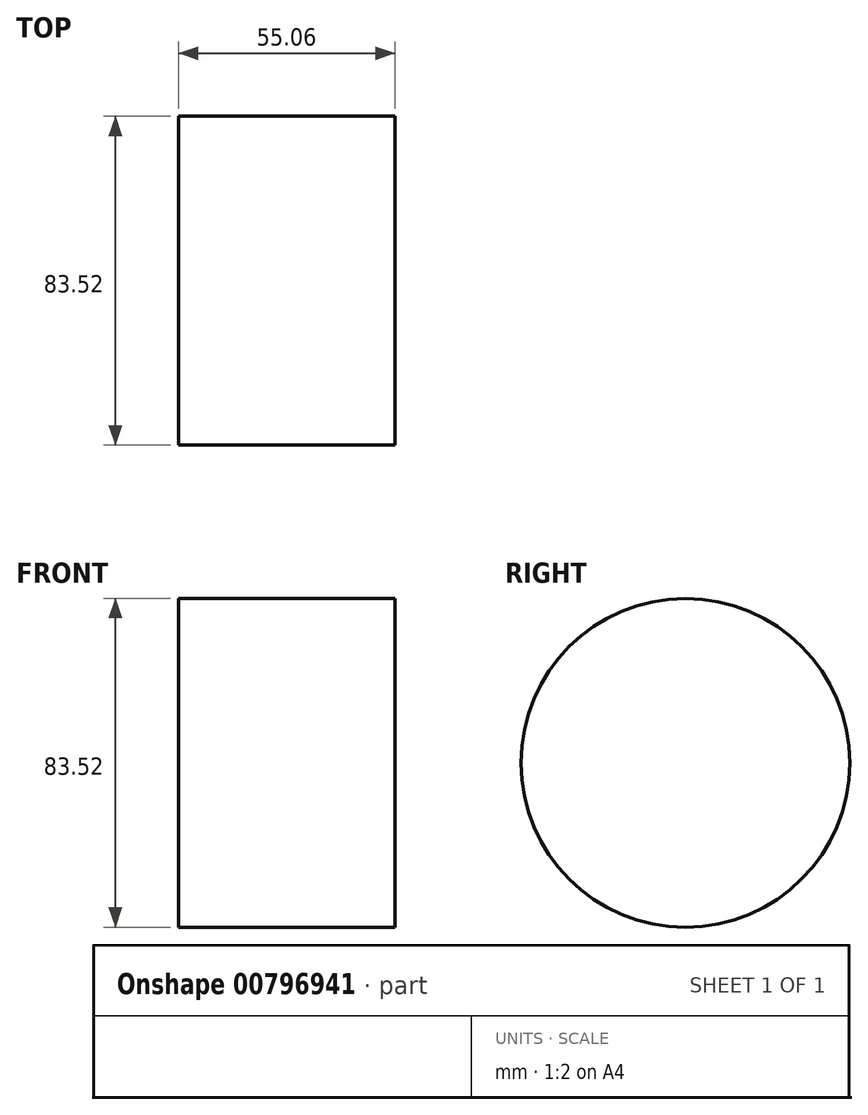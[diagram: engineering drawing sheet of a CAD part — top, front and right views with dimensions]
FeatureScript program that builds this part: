
annotation { "Feature Type Name" : "Feature", "Feature Type Description" : "" }
export const myFeature = defineFeature(function(context is Context, id is Id, definition is map)
    precondition{}
    {
        {
            var Q0;
            Q0=qCreatedBy(makeId("Front.planeOp"),FACE);
            var sketch = newSketch(context, id + "F0", { "sketchPlane" : qUnion([Q0])});
            skLineSegment(sketch, "E0", {"start": v(0, 0) * mm, "end": v(0, 41.76) * mm});
            skLineSegment(sketch, "E1", {"start": v(0, 41.76) * mm, "end": v(55.06, 41.76) * mm});
            skLineSegment(sketch, "E2", {"start": v(55.06, 41.76) * mm, "end": v(55.06, 0) * mm});
            skLineSegment(sketch, "E3", {"start": v(55.06, 0) * mm, "end": v(0, 0) * mm});
            skSolve(sketch);
        }
        {
            var Q0;
            Q0=sQuery(id+"F0.wireOp",EDGE,"E0");
            var Q1;
            Q1=sQuery(id+"F0.wireOp",EDGE,"E2");
            var Q2;
            Q2=sQuery(id+"F0.wireOp",EDGE,"E3");
            var Q3;
            Q3=sQuery(id+"F0.wireOp",EDGE,"E1");
            revolve(context, id + "F1", {"bodyType" : ToolBodyType.SURFACE, "surfaceOperationType" : NewSurfaceOperationType.NEW, "surfaceEntities" : qUnion([Q0, Q1, Q2]), "axis" : qUnion([Q3]), "revolveType" : RevolveType.FULL});
        }
        {
            var Q0;
            Q0=makeQuery(id+"F0.imprint","IMPRINT",FACE,{"disambiguationData":[TD([[makeQuery(id+"F0.imprint","IMPRINT",EDGE,{"derivedFrom":sQuery(id+"F0.wireOp",EDGE,"E0")}),-1.0]])]});
            var Q1;
            Q1=sQuery(id+"F0.wireOp",EDGE,"E3");
            revolve(context, id + "F2", {"surfaceOperationType" : NewSurfaceOperationType.NEW, "entities" : qUnion([Q0]), "axis" : qUnion([Q1]), "revolveType" : RevolveType.FULL});
        }
    });
